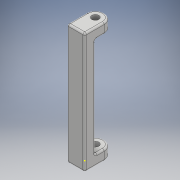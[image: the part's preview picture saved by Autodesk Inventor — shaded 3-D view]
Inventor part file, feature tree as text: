
AUTODESK INVENTOR PART (.ipt)
format: ipt  version: 2018 (Build 220112000, 112)  size: 176,128 bytes
history: native  units: mm
features: sketch x5, extrude x4, fillet x2
ambient origin geometry x8: Origin, YZ Plane, XZ Plane, XY Plane, X Axis, Y Axis, Z Axis, Center Point
bodies: Solid1 (feature_tree)
feature tree (11):
  extrude  "Extrusion1"  Depth=34.0mm
  extrude  "Extrusion2"  Depth=3.0mm
  fillet  "Fillet1"  Radius=5.0mm
  sketch  "Sketch3"  dims[d6=3.0mm d7=5.0mm d8=0.0mm]
  sketch  "Sketch4"  dims[d9=2.5mm d10=2.0mm d11=0.0mm]
  extrude  "Extrusion3"  Depth=5.0mm TaperAngle=0.0deg
  extrude  "Extrusion4"  Depth=2.0mm
  fillet  "Fillet2"  [1 undecoded]
  sketch  "Sketch1"  dims[d0=5.0mm d1=34.0mm]
  sketch  "Sketch2"  dims[d2=3.0mm d3=0.0mm d4=3.0mm d5=5.0mm]
  sketch  "Sketch5"  dims[d12=2.5mm d13=2.0mm d14=0.0mm d15=2.5mm d16=3.0mm d17=0.0mm d18=3.0mm d19=0.0mm d20=0.5mm]
note: 1 required parameter value undecoded (feature->parameter linkage not recoverable at this tier; creation-order binding heuristic only, values carry confidence <= 0.55)
